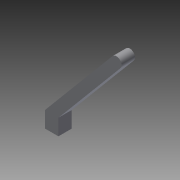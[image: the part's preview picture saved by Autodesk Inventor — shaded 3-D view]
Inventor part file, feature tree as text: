
AUTODESK INVENTOR PART (.ipt)
format: ipt  version: 2013 (Build 170138000, 138)  size: 73,728 bytes
history: native  units: in
note: dims shown in document units (in); Inventor stores cm internally (conversion verified against a paired STEP export)
features: extrude x1, sketch x1
ambient origin geometry x8: Origin, YZ Plane, XZ Plane, XY Plane, X Axis, Y Axis, Z Axis, Center Point
bodies: Solid1 (feature_tree)
feature tree (2):
  extrude  "Extrusion1"  Depth=0.25in
  sketch  "Sketch1"  dims[d0=0.3in d1=0.25in d2=0.3436in d3=1.5in d4=1.7974in d5=0.0958in d6=0.25in d7=0.0in]
